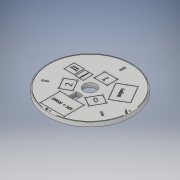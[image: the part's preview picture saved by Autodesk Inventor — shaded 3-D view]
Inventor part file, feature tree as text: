
AUTODESK INVENTOR PART (.ipt)
format: ipt  version: 2019 (Build 230136000, 136)  size: 2,276,352 bytes
history: native  units: mm
features: sketch x12, projected_geometry x8, extrude x5, hole x5, pattern_circular x2, emboss x2
ambient origin geometry x8: Origin, YZ Plane, XZ Plane, XY Plane, X Axis, Y Axis, Z Axis, Center Point
bodies: Solid1 (feature_tree)
feature tree (34):
  extrude  "Extrusion1"  Depth=30.0mm
  hole  "Hole1"  [1 undecoded]
  pattern_circular  "Circular Pattern1"  Count=3  [1 undecoded]
  hole  "Hole2"  [1 undecoded]
  hole  "Hole3"  [1 undecoded]
  hole  "Hole4"  [1 undecoded]
  emboss  "Emboss1"
  extrude  "Extrusion2"  Depth=25.0mm
  extrude  "Extrusion3"  Depth=2.0mm
  hole  "Hole5"  [1 undecoded]
  emboss  "Emboss2"
  extrude  "Extrusion4"  Depth=1.0mm
  pattern_circular  "Circular Pattern2"  [2 undecoded]
  extrude  "Extrusion5"  Depth=1.0mm
  sketch  "Sketch1"  dims[d0=200.0mm d1=30.0mm]
  sketch  "Sketch2"  dims[d2=10.0mm d3=0.0mm d4=38.0mm d5=30.0mm]
  projected_geometry  "Projected Loop1"
  sketch  "Sketch3"  dims[d6=24.0mm]
  projected_geometry  "Projected Loop2"
  sketch  "Sketch4"  dims[d7=4.0mm d8=6.0mm d9=4.0mm d10=2.0mm d11=90.0deg d12=8.0mm d13=20.594885mm d14=30.0mm d15=360.0deg]
  projected_geometry  "Projected Loop3"
  sketch  "Sketch5"  dims[d17=34.0mm d18=58.0mm]
  projected_geometry  "Projected Loop4"
  sketch  "Sketch6"  dims[d19=48.0mm]
  sketch  "Sketch7"  dims[d20=2.5mm d21=6.0mm d22=4.0mm d23=2.0mm d24=90.0deg d25=8.0mm d26=20.594885mm d27=40.0mm]
  sketch  "Sketch8"  dims[d28=25.0mm d29=25.0mm]
  sketch  "Sketch9"  dims[d30=2.5mm d31=6.0mm d32=4.0mm d33=2.0mm d34=90.0deg d35=8.0mm d36=20.594885mm d37=12.25mm]
  sketch  "Sketch10"  dims[d38=12.25mm]
  sketch  "Sketch11"  dims[d39=1.6mm d40=6.0mm d41=4.0mm d42=2.0mm d43=90.0deg d44=8.0mm d45=20.594885mm d46=6.0mm]
  sketch  "Sketch12"  dims[d47=6.0mm d48=73.245191mm d49=32.174mm d50=25.0mm d51=25.0mm d52=1.0mm d53=0.0mm d54=16.0mm d55=20.0mm d56=10.0mm d57=0.0mm d58=1.0mm d59=10.0mm d60=24.5mm d61=10.0mm d62=24.5mm d63=1.0mm d64=1.0mm d65=1.0mm d66=30.0mm d68=360.0deg d70=20.0mm d71=20.0mm d72=1.0mm d73=1.0mm d74=0.0mm d75=95.0mm d76=0.0mm d77=95.0mm d78=4.0mm d79=4.0mm d80=6.0mm d81=4.0mm d82=2.0mm d83=90.0deg d84=8.0mm d85=20.594885mm d86=15.0mm d87=15.0mm d88=20.0mm d89=9.0mm d90=1.0mm d91=0.0mm d92=27.0mm d93=30.0deg d94=5.0mm d95=4.0mm d96=1.0mm d97=0.0mm d98=30.0mm d99=360.0deg d101=1.5mm d102=1.745329mm d103=1.745329mm d104=1.745329mm d105=1.745329mm d106=98.5mm d107=98.5mm d108=17.104346mm d109=98.5mm d110=1.0mm d111=1.0mm d112=1.0mm d113=0.0mm]
  projected_geometry  "Project Cut Edges1"
  projected_geometry  "Project Cut Edges2"
  projected_geometry  "Project Cut Edges3"
  projected_geometry  "Project Cut Edges4"
note: 8 required parameter values undecoded (feature->parameter linkage not recoverable at this tier; creation-order binding heuristic only, values carry confidence <= 0.55)
